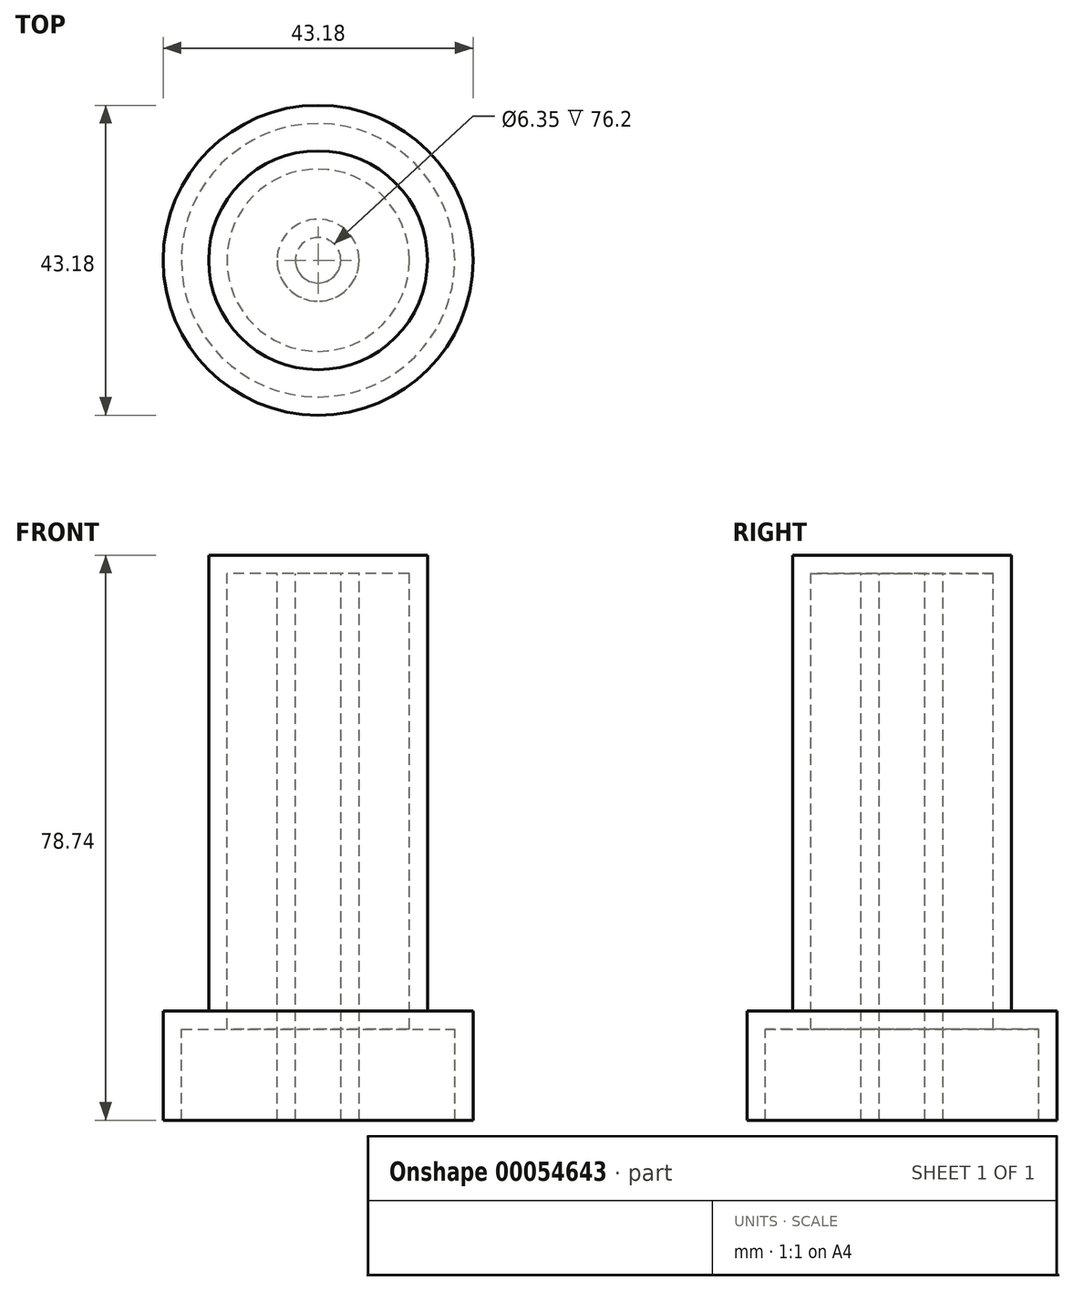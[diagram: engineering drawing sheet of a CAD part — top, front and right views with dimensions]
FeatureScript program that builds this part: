
annotation { "Feature Type Name" : "Feature", "Feature Type Description" : "" }
export const myFeature = defineFeature(function(context is Context, id is Id, definition is map)
    precondition{}
    {
        {
            var Q0;
            Q0=qCreatedBy(makeId("Top.planeOp"),FACE);
            var sketch = newSketch(context, id + "F0", { "sketchPlane" : qUnion([Q0])});
            skCircle(sketch, "E0", {"center": v(0, 0) * mm, "radius": 12.7 * mm});
            skSolve(sketch);
        }
        {
            var Q0;
            Q0=makeQuery(id+"F0.imprint","IMPRINT",FACE,{"disambiguationData":[TD([[makeQuery(id+"F0.imprint","IMPRINT",EDGE,{"derivedFrom":sQuery(id+"F0.wireOp",EDGE,"E0")}),1.0]])]});
            extrude(context, id + "F1", {"entities" : qUnion([Q0]), "oppositeDirection" : true, "depth" : 63.5 * mm});
        }
        {
            var Q0;
            Q0=makeQuery(id+"F1.opExtrude","CAP_FACE",FACE,{"disambiguationData":[OSD([sQuery(id+"F0.wireOp",EDGE,"E0")])],"isStart":false});
            var sketch = newSketch(context, id + "F2", { "sketchPlane" : qUnion([Q0])});
            skCircle(sketch, "E1", {"center": v(0, 0) * mm, "radius": 19.05 * mm});
            skSolve(sketch);
        }
        {
            var Q0;
            Q0 = qSketchRegion(id + "F2", true);
            extrude(context, id + "F3", {"entities" : qUnion([Q0]), "operationType" : NewBodyOperationType.ADD, "depth" : 12.7 * mm});
        }
        {
            var Q0;
            Q0=makeQuery(id+"F3.opExtrude","CAP_FACE",FACE,{"disambiguationData":[OSD([sQuery(id+"F2.wireOp",EDGE,"E1")])],"isStart":false});
            shell(context, id + "F4", {"entities" : qUnion([Q0]), "thickness" : 2.54 * mm, "oppositeDirection" : true});
        }
        {
            var Q0;
            Q0=makeQuery(id+"F1.opExtrude","CAP_FACE",FACE,{"disambiguationData":[OSD([sQuery(id+"F0.wireOp",EDGE,"E0")])],"isStart":true});
            var sketch = newSketch(context, id + "F5", { "sketchPlane" : qUnion([Q0])});
            skCircle(sketch, "E2", {"center": v(0, 0) * mm, "radius": 3.18 * mm});
            skCircle(sketch, "E3", {"center": v(0, 0) * mm, "radius": 5.72 * mm});
            skSolve(sketch);
        }
        {
            var Q0;
            Q0=makeQuery(id+"F5.imprint","IMPRINT",FACE,{"disambiguationData":[TD([[makeQuery(id+"F5.imprint","IMPRINT",EDGE,{"derivedFrom":sQuery(id+"F5.wireOp",EDGE,"E2")}),-1.0]])]});
            var Q1;
            Q1=makeQuery(id+"F3.opExtrude","CAP_FACE",FACE,{"disambiguationData":[OSD([sQuery(id+"F2.wireOp",EDGE,"E1")])],"isStart":false});
            extrude(context, id + "F6", {"entities" : qUnion([Q0]), "operationType" : NewBodyOperationType.ADD, "endBound" : BoundingType.UP_TO_SURFACE, "oppositeDirection" : true, "endBoundEntityFace" : qUnion([Q1]), "depth" : 25.4 * mm});
        }
    });
